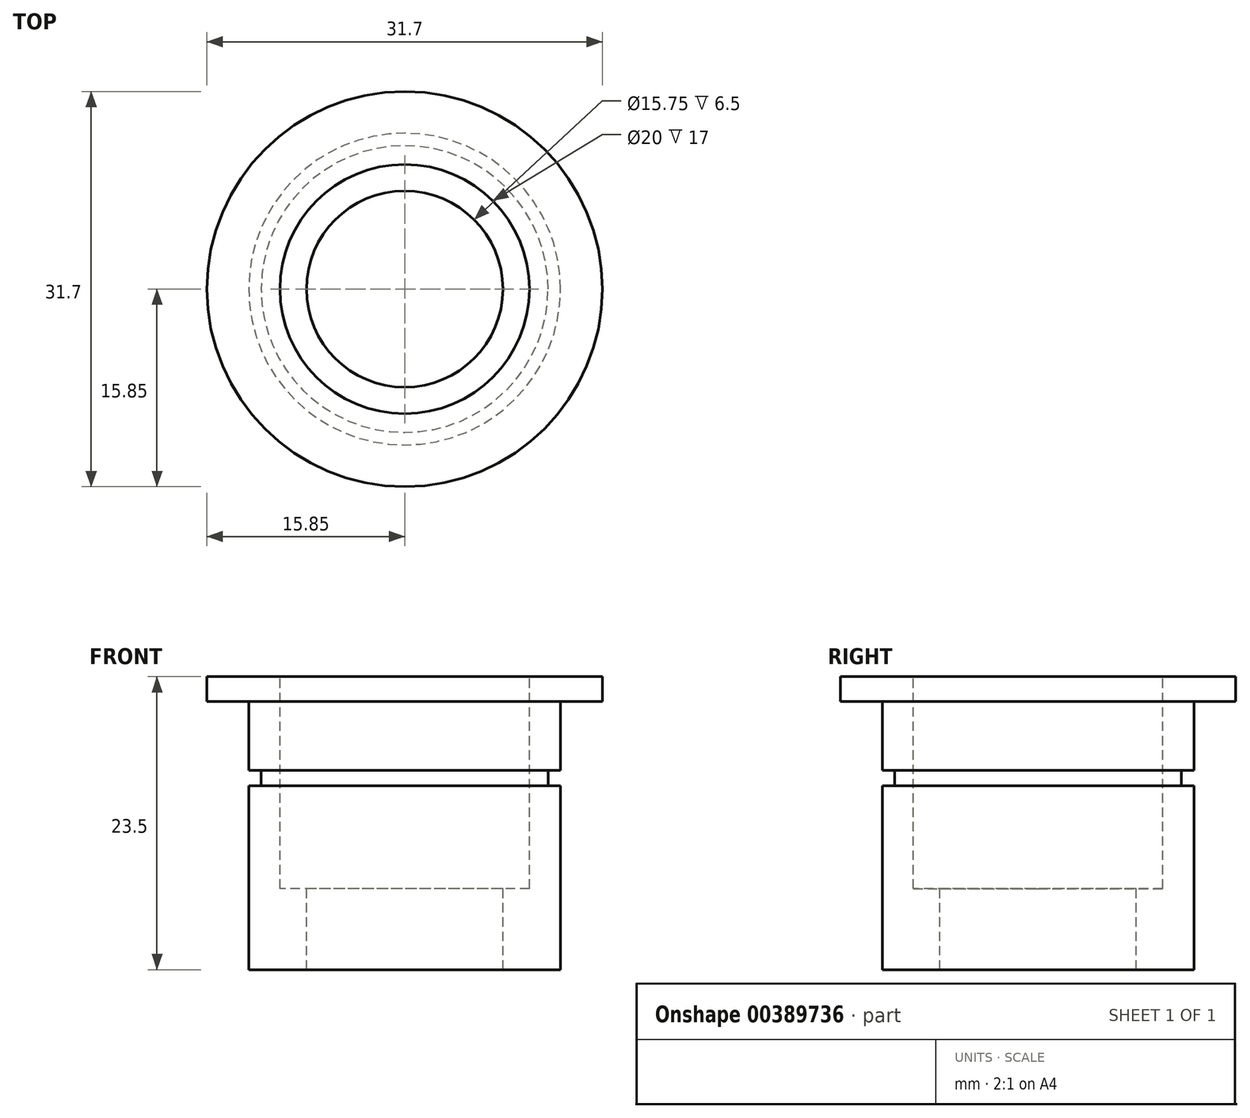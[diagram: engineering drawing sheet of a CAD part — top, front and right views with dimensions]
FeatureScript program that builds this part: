
annotation { "Feature Type Name" : "Feature", "Feature Type Description" : "" }
export const myFeature = defineFeature(function(context is Context, id is Id, definition is map)
    precondition{}
    {
        {
            var Q0;
            Q0=qCreatedBy(makeId("Top.planeOp"),FACE);
            var sketch = newSketch(context, id + "F0", { "sketchPlane" : qUnion([Q0])});
            skCircle(sketch, "E0", {"center": v(0, 0) * mm, "radius": 12.5 * mm});
            skSolve(sketch);
        }
        {
            var Q0;
            Q0=makeQuery(id+"F0.imprint","IMPRINT",FACE,{"disambiguationData":[TD([[makeQuery(id+"F0.imprint","IMPRINT",EDGE,{"derivedFrom":sQuery(id+"F0.wireOp",EDGE,"E0")}),1.0]])]});
            extrude(context, id + "F1", {"entities" : qUnion([Q0]), "depth" : 21.5 * mm});
        }
        {
            var Q0;
            Q0=makeQuery(id+"F1.opExtrude","CAP_FACE",FACE,{"disambiguationData":[OSD([sQuery(id+"F0.wireOp",EDGE,"E0")])],"isStart":false});
            var sketch = newSketch(context, id + "F2", { "sketchPlane" : qUnion([Q0])});
            skCircle(sketch, "E1", {"center": v(0, 0) * mm, "radius": 15.85 * mm});
            skSolve(sketch);
        }
        {
            var Q0;
            Q0=makeQuery(id+"F2.imprint","IMPRINT",FACE,{"disambiguationData":[TD([[makeQuery(id+"F2.imprint","IMPRINT",EDGE,{"derivedFrom":makeQuery(id+"F1.opExtrude","CAP_EDGE",EDGE,{"disambiguationData":[OSD([sQuery(id+"F0.wireOp",EDGE,"E0")])],"isStart":false})}),1.0]])]});
            var Q1;
            Q1=makeQuery(id+"F2.imprint","IMPRINT",FACE,{"disambiguationData":[TD([[makeQuery(id+"F2.imprint","IMPRINT",EDGE,{"derivedFrom":sQuery(id+"F2.wireOp",EDGE,"E1")}),1.0]])]});
            extrude(context, id + "F3", {"entities" : qUnion([Q0, Q1]), "operationType" : NewBodyOperationType.ADD, "depth" : 2 * mm});
        }
        {
            var Q0;
            Q0=makeQuery(id+"F3.opExtrude","CAP_FACE",FACE,{"disambiguationData":[OSD([sQuery(id+"F2.wireOp",EDGE,"E1")])],"isStart":false});
            var sketch = newSketch(context, id + "F4", { "sketchPlane" : qUnion([Q0])});
            skPoint(sketch, "E2", {"position": v(0, 0) * mm});
            skSolve(sketch);
        }
        {
            var Q0;
            Q0=sQuery(id+"F4.wireOp",VERTEX,"E2");
            var Q1;
            Q1=makeQuery(id+"F1.opExtrude","SWEPT_BODY",BODY,{"disambiguationData":[OSD([sQuery(id+"F0.wireOp",EDGE,"E0")])]});
            hole(context, id + "F5", {"style" : HoleStyle.SIMPLE, "endStyle" : HoleEndStyle.BLIND, "holeDiameter" : 15.75 * mm, "holeDepth" : 23.5 * mm, "isTappedThrough" : true, "tappedDepth" : 12 * mm, "tapClearance" : 3, "locations" : qUnion([Q0]), "scope" : qUnion([Q1])});
        }
        {
            var Q0;
            Q0=makeQuery(id+"F4.imprint","IMPRINT",FACE,{"disambiguationData":[TD([[makeQuery(id+"F4.imprint","IMPRINT",EDGE,{"derivedFrom":makeQuery(id+"F3.opExtrude","CAP_EDGE",EDGE,{"disambiguationData":[OSD([sQuery(id+"F2.wireOp",EDGE,"E1")])],"isStart":false})}),1.0]])]});
            var sketch = newSketch(context, id + "F6", { "sketchPlane" : qUnion([Q0])});
            skCircle(sketch, "E3", {"center": v(0, 0) * mm, "radius": 10 * mm});
            skSolve(sketch);
        }
        {
            var Q0;
            Q0 = qSketchRegion(id + "F6", true);
            extrude(context, id + "F7", {"entities" : qUnion([Q0]), "operationType" : NewBodyOperationType.REMOVE, "oppositeDirection" : true, "depth" : (17) * mm});
        }
        {
            var Q0;
            Q0=qCreatedBy(makeId("Front.planeOp"),FACE);
            var sketch = newSketch(context, id + "F8", { "sketchPlane" : qUnion([Q0])});
            skLineSegment(sketch, "E4", {"start": v(0, 0) * mm, "end": v(0, 16) * mm, "construction": true});
            skLineSegment(sketch, "E5", {"start": v(0, 16) * mm, "end": v(-12.5, 16) * mm, "construction": true});
            skLineSegment(sketch, "E6", {"start": v(-12.5, 16) * mm, "end": v(-12.5, 14.75) * mm});
            skLineSegment(sketch, "E7", {"start": v(-12.5, 14.75) * mm, "end": v(-11.5, 14.75) * mm});
            skLineSegment(sketch, "E8", {"start": v(-11.5, 14.75) * mm, "end": v(-11.5, 16) * mm});
            skLineSegment(sketch, "E9", {"start": v(-11.5, 16) * mm, "end": v(-12.5, 16) * mm});
            skSolve(sketch);
        }
        {
            var Q0;
            Q0 = qSketchRegion(id + "F8", true);
            var Q1;
            Q1=sQuery(id+"F8.wireOp",EDGE,"E4");
            revolve(context, id + "F9", {"operationType" : NewBodyOperationType.REMOVE, "entities" : qUnion([Q0]), "axis" : qUnion([Q1]), "revolveType" : RevolveType.FULL, "oppositeDirection" : true});
        }
    });
